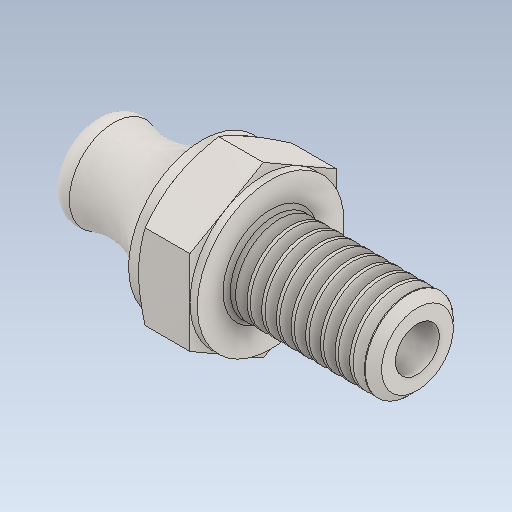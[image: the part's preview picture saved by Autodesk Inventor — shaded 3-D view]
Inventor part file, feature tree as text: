
AUTODESK INVENTOR PART (.ipt)
format: ipt  version: 2021 (Build 250183000, 183)  size: 248,832 bytes
history: mixed  units: mm
features: other x1, fillet x1, imported_body x1
ambient origin geometry x8: Origin, YZ Plane, XZ Plane, XY Plane, X Axis, Y Axis, Z Axis, Center Point
bodies: Body1 (imported_parasolid)
feature tree (3):
  other  "Sólido1"
  fillet  "Fillet1"  [1 undecoded]
  imported_body  NMx_Import_Brep_tag  [imported B-rep: ~21 faces, bbox_mm=[1.111735, 8.773503, 10.0]]
note: 1 required parameter value undecoded (feature->parameter linkage not recoverable at this tier; creation-order binding heuristic only, values carry confidence <= 0.55)
